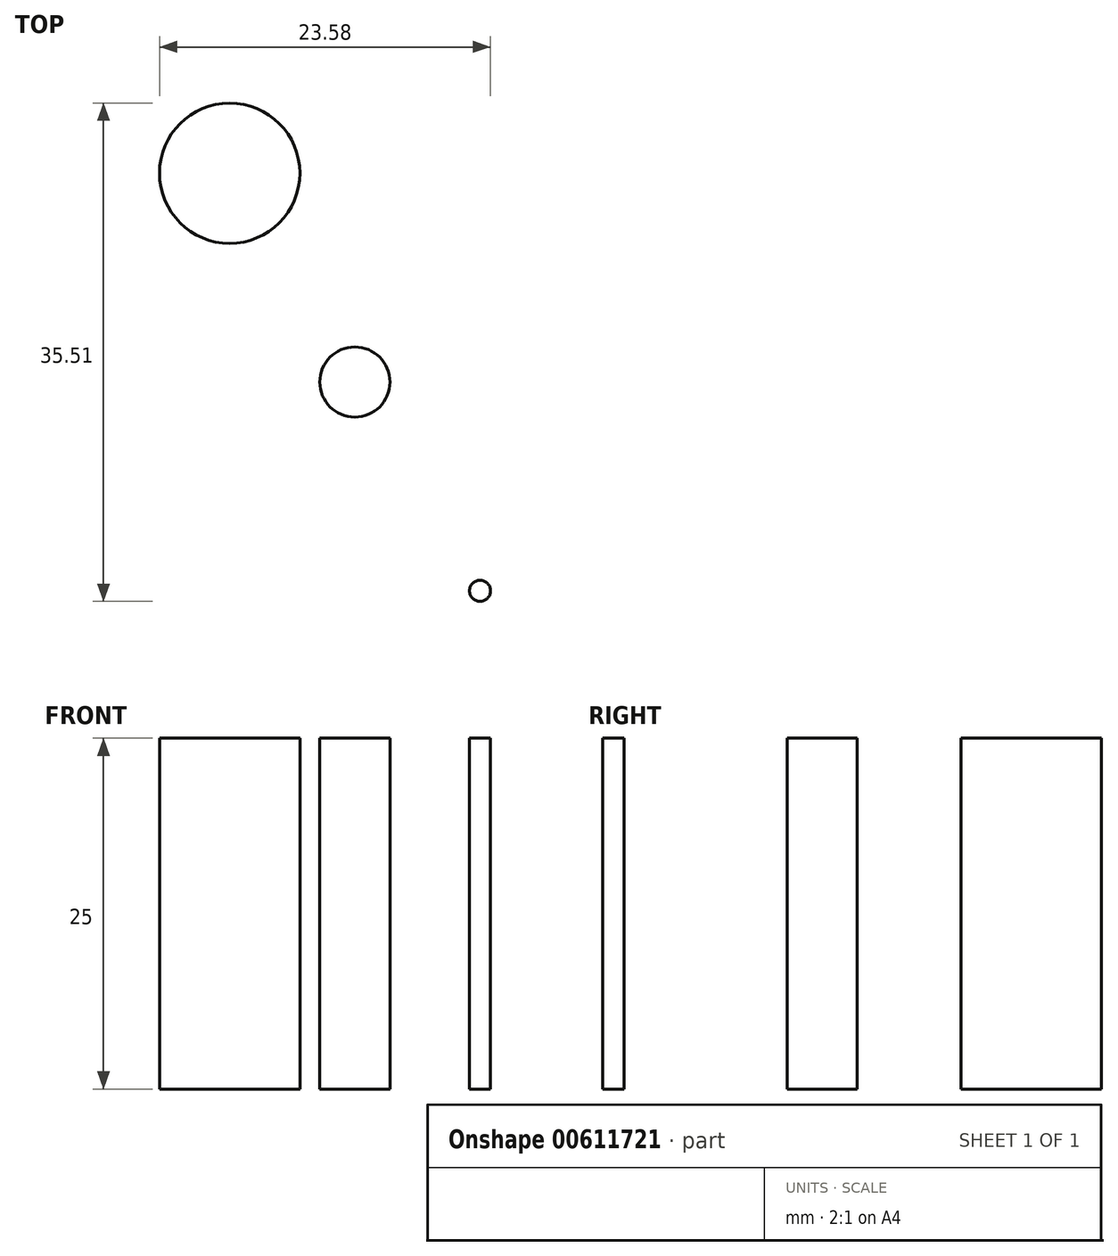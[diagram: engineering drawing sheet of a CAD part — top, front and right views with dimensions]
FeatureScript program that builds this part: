
annotation { "Feature Type Name" : "Feature", "Feature Type Description" : "" }
export const myFeature = defineFeature(function(context is Context, id is Id, definition is map)
    precondition{}
    {
        {
            var Q0;
            Q0=qCreatedBy(makeId("Top.planeOp"),FACE);
            var sketch = newSketch(context, id + "F0", { "sketchPlane" : qUnion([Q0])});
            skCircle(sketch, "E0", {"center": v(0, 0) * mm, "radius": 0.75 * mm});
            skLineSegment(sketch, "E1", {"start": v(0, 0) * mm, "end": v(-17.83, 29.76) * mm, "construction": true});
            skCircle(sketch, "E2", {"center": v(-8.92, 14.88) * mm, "radius": 2.5 * mm});
            skCircle(sketch, "E3", {"center": v(-17.83, 29.76) * mm, "radius": 5 * mm});
            skSolve(sketch);
        }
        {
            var Q0;
            Q0=makeQuery(id+"F0.imprint","IMPRINT",FACE,{"disambiguationData":[TD([[makeQuery(id+"F0.imprint","IMPRINT",EDGE,{"derivedFrom":sQuery(id+"F0.wireOp",EDGE,"E0")}),1.0]])]});
            var Q1;
            Q1=makeQuery(id+"F0.imprint","IMPRINT",FACE,{"disambiguationData":[TD([[makeQuery(id+"F0.imprint","IMPRINT",EDGE,{"derivedFrom":sQuery(id+"F0.wireOp",EDGE,"E2")}),1.0]])]});
            var Q2;
            Q2=makeQuery(id+"F0.imprint","IMPRINT",FACE,{"disambiguationData":[TD([[makeQuery(id+"F0.imprint","IMPRINT",EDGE,{"derivedFrom":sQuery(id+"F0.wireOp",EDGE,"E3")}),1.0]])]});
            extrude(context, id + "F1", {"entities" : qUnion([Q0, Q1, Q2]), "depth" : 25 * mm, "offsetDistance" : 25 * mm});
        }
    });
